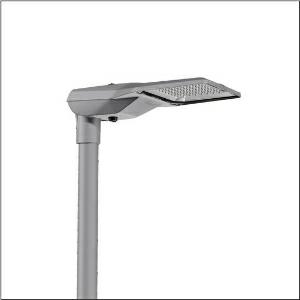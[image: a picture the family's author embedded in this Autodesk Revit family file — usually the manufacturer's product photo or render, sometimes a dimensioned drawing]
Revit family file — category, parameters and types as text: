
# Revit family: streetlight_sl_21_iq_midi___st1_0a_5xe3d21y08nb_2a15
name_source: partatom
category: Lighting Fixtures
units: mm (PartAtom-declared; Revit-internal decimal feet)

## family parameters
Cut with Voids When Loaded = No
Host = Face
Light Source = No
Part Type = Normal
Room Calculation Point = No
Round Connector Dimension = Use Diameter
Shared = No

## types (1)
- --- (1 x LED, 17280 lm, 136.6 W, 2200K)
    Apparent Load = 137 VA
    CIE Flux Codes = 40 73 97 100 100
    Color Rendering = 70
    Color Temperature = 2200K
    Default Elevation = 1800 mm
    Description = Streetlight SL 21 iQ midi, mast luminaire, primary light control with lens, of PMMA, primary optical cover: cover, of toughened safety glass, transparent, light distribution: ST1.0a, light emission: direct distribution, primary light characteristic: asymmetric, installation type: post-top, side-entry, LED, High Power LED, rated luminous flux: 17.280lm, luminous efficacy: 127lm/W, light colour: 722, colour temperature: 2200K, control gear: iQ-Street Remote, D4i with power reduction, control: pre-setting: logarithmic dimming characteristic, Street-Remote, Auto-Match, Temp-Guard, Lumen-Switch, Night-Set, Smart-Wire, Light-Fading, Desk-Remote (wireless, voltage-free reading and setting of iQ features in the workshop via application-optimized NFC function/RFID function), optimised constant luminous flux control (CLO 2.0), mains connection: 230..240V, AC, 50/60Hz, start of lifetime: 137W, end of service life: 144W, reduction: 61W, luminaire housing, of diecast aluminium, powder-coated, SITECO metallic grey (DB 702S), corrosivity category C5 high according to DIN EN ISO 12944, please order mast flange separately, inclination adjustable: 0°, 5°, 10°, 15°, sealing non-destructively replaceable, multi-level sealing system, length: 644mm, width: 335mm, height: 110mm, mast flange for spigot size: 42mm (side-entry): 5XC10008XM4, 60/48mm (side-entry/post-top): 5XC10108XM2, 76/60mm (side-entry/post-top): 5XC10108XM1, mounting height: 4..8m, Smart Interface below and above, protection rating (complete): IP66, insulation class (complete): insulation class II (safety insulation), certification: CE, ENEC, ENEC+, VDE, impact resistance: IK10, permissible operating ambient temperature for outdoor applications: -40..+50°C, standard-compliant lighting for roads and squares, packaging unit: 1 piece

Light Distribution: ST1.0a
    Height = 111 mm
    Lamp = 1 x LED
    Lamp Light Flux = 17280 lm
    Lamp Power = 136.6 W
    Lamp count = 1
    Length = 644 mm
    Luminous efficacy = 127 lm/W
    Manufacturer = Siteco
    ModVariant = No
    Model = 5XE3D21Y08NB
    Number of Poles = 1
    OnlyDefault = Yes
    Power Factor = 1
    Product Name = Streetlight SL 21 iQ midi | ST1.0a
    Product group = mast luminaire | pylon top
    ProductGroupID = 6100
    Protection Class = Protection class II
    Protection Degree = IP 66
    RLX_Detail_Level = 1
    RLX_Emergency_Light_Flux = 0 lm
    RLX_Emergency_Type = 0
    RLX_Emergency_Type_DB = No
    RlxData = <blob elided: 91153 chars, md5=68daeaa3>
    Socket = socket
    Standby Power = 0 W
    System Light Flux = 17280 lm
    System Power = 137 W
    Type Comments = factory setting: luminous flux: 100 % | dim-lin: 254 | 733 mA
    Type Image = l_1004304.jpg
    URL = http://relux.com
    VarID = @adj_114005
    Voltage = 0 V
    Weight = 0.00 kg
    Width = 336 mm

## geometry (parser evidence)
native form markers: Blend x4, Sweep x13
no freeform markers — native parametric forms only
